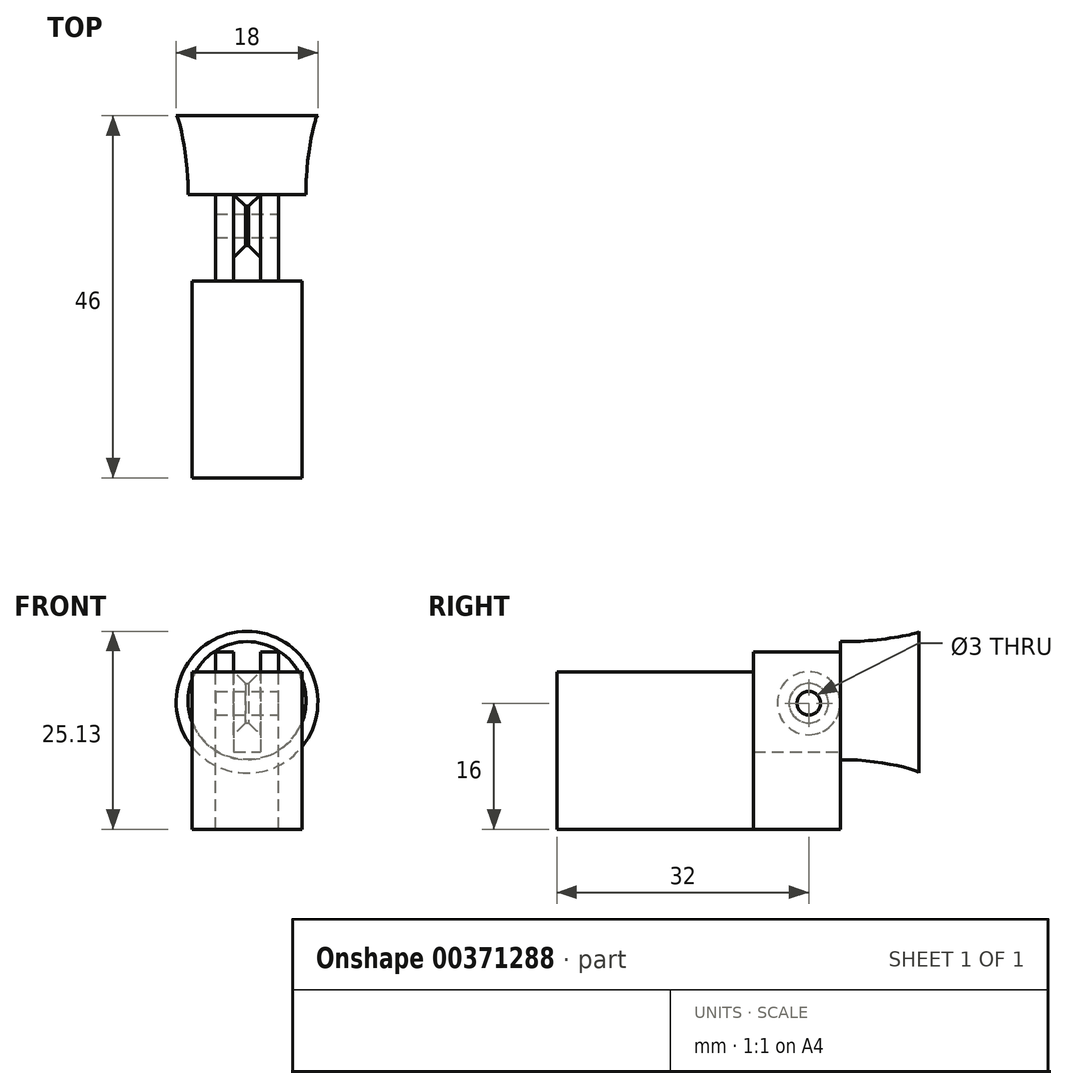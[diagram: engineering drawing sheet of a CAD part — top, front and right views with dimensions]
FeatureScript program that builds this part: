
annotation { "Feature Type Name" : "Feature", "Feature Type Description" : "" }
export const myFeature = defineFeature(function(context is Context, id is Id, definition is map)
    precondition{}
    {
        {
            var Q0;
            Q0=qCreatedBy(makeId("Front.planeOp"),FACE);
            var sketch = newSketch(context, id + "F0", { "sketchPlane" : qUnion([Q0])});
            skLineSegment(sketch, "E0", {"start": v(0, 0) * mm, "end": v(-4, 0) * mm});
            skLineSegment(sketch, "E1", {"start": v(-4, 0) * mm, "end": v(-4, 22.5) * mm});
            skLineSegment(sketch, "E2", {"start": v(-4, 22.5) * mm, "end": v(-1.7, 22.5) * mm});
            skLineSegment(sketch, "E3", {"start": v(-1.7, 22.5) * mm, "end": v(-1.7, 0) * mm, "construction": true});
            skPoint(sketch, "E3.endSnap0", {"position": v(-2, 0) * mm});
            skLineSegment(sketch, "E4", {"start": v(-1.7, 0) * mm, "end": v(-1.7, 9.8) * mm, "construction": true});
            skLineSegment(sketch, "E5", {"start": v(-1.7, 22.5) * mm, "end": v(-1.7, 9.8) * mm});
            skLineSegment(sketch, "E6", {"start": v(-1.7, 9.8) * mm, "end": v(0, 9.8) * mm});
            skLineSegment(sketch, "E7", {"start": v(0, 9.8) * mm, "end": v(0, 0) * mm});
            skSolve(sketch);
        }
        {
            var Q0;
            Q0=makeQuery(id+"F0.imprint","IMPRINT",FACE,{"disambiguationData":[TD([[makeQuery(id+"F0.imprint","IMPRINT",EDGE,{"derivedFrom":sQuery(id+"F0.wireOp",EDGE,"E0")}),-1.0]])]});
            extrude(context, id + "F1", {"entities" : qUnion([Q0]), "depth" : 11 * mm});
        }
        {
            var Q0;
            Q0=makeQuery(id+"F1.opExtrude","SWEPT_BODY",BODY,{"disambiguationData":[OSD([sQuery(id+"F0.wireOp",EDGE,"E0"),sQuery(id+"F0.wireOp",EDGE,"E1"),sQuery(id+"F0.wireOp",EDGE,"E2"),sQuery(id+"F0.wireOp",EDGE,"E5"),sQuery(id+"F0.wireOp",EDGE,"E6"),sQuery(id+"F0.wireOp",EDGE,"E7")])]});
            var Q1;
            Q1=makeQuery(id+"F1.opExtrude","SWEPT_FACE",FACE,{"disambiguationData":[OSD([sQuery(id+"F0.wireOp",EDGE,"E7")])]});
            mirror(context, id + "F2", {"operationType" : NewBodyOperationType.ADD, "entities" : qUnion([Q0]), "mirrorPlane" : qUnion([Q1])});
        }
        {
            var Q0;
            {var subQ0=makeQuery(id+"F1.opExtrude","CAP_FACE",FACE,{"disambiguationData":[OSD([sQuery(id+"F0.wireOp",EDGE,"E0"),sQuery(id+"F0.wireOp",EDGE,"E1"),sQuery(id+"F0.wireOp",EDGE,"E2"),sQuery(id+"F0.wireOp",EDGE,"E5"),sQuery(id+"F0.wireOp",EDGE,"E6"),sQuery(id+"F0.wireOp",EDGE,"E7")])],"isStart":false});Q0=makeQuery(id+"F2.boolean.opBoolean","MERGE",FACE,{"derivedFrom":[subQ0,makeQuery(id+"F2.opPattern","COPY",FACE,{"derivedFrom":subQ0,"instanceName":"1"})]});}
            var sketch = newSketch(context, id + "F3", { "sketchPlane" : qUnion([Q0])});
            skLineSegment(sketch, "E8", {"start": v(0, 0) * mm, "end": v(-7, 0) * mm, "construction": true});
            skLineSegment(sketch, "E9", {"start": v(0, 0) * mm, "end": v(-7, 0) * mm});
            skLineSegment(sketch, "E10", {"start": v(-7, 0) * mm, "end": v(-7, 20) * mm});
            skLineSegment(sketch, "E11", {"start": v(0, 0) * mm, "end": v(7, 0) * mm});
            skLineSegment(sketch, "E12", {"start": v(7, 0) * mm, "end": v(7, 20) * mm});
            skLineSegment(sketch, "E13", {"start": v(-7, 20) * mm, "end": v(7, 20) * mm});
            skSolve(sketch);
        }
        {
            var Q0;
            {var subQ3=sQuery(id+"F3.wireOp",EDGE,"E12");Q0=makeQuery(id+"F3.imprint","IMPRINT",FACE,{"disambiguationData":[TD([[makeQuery(id+"F3.imprint","IMPRINT",EDGE,{"derivedFrom":subQ3}),1.0]])]});}
            var Q1;
            {var subQ13=makeQuery(id+"F1.opExtrude","CAP_EDGE",EDGE,{"disambiguationData":[OSD([sQuery(id+"F0.wireOp",EDGE,"E6")])],"isStart":false});var subQ14=makeQuery(id+"F2.boolean.opBoolean","MERGE",EDGE,{"derivedFrom":[subQ13,makeQuery(id+"F2.opPattern","COPY",EDGE,{"derivedFrom":subQ13,"instanceName":"1"})]});Q1=makeQuery(id+"F3.imprint","IMPRINT",FACE,{"disambiguationData":[TD([[makeQuery(id+"F3.imprint","IMPRINT",EDGE,{"derivedFrom":subQ14}),-1.0]])]});}
            var Q2;
            {var subQ5=makeQuery(id+"F1.opExtrude","CAP_EDGE",EDGE,{"disambiguationData":[OSD([sQuery(id+"F0.wireOp",EDGE,"E6")])],"isStart":false});var subQ6=makeQuery(id+"F2.boolean.opBoolean","MERGE",EDGE,{"derivedFrom":[subQ5,makeQuery(id+"F2.opPattern","COPY",EDGE,{"derivedFrom":subQ5,"instanceName":"1"})]});Q2=makeQuery(id+"F3.imprint","IMPRINT",FACE,{"disambiguationData":[TD([[makeQuery(id+"F3.imprint","IMPRINT",EDGE,{"derivedFrom":subQ6}),1.0]])]});}
            var Q3;
            {var subQ3=sQuery(id+"F3.wireOp",EDGE,"E10");Q3=makeQuery(id+"F3.imprint","IMPRINT",FACE,{"disambiguationData":[TD([[makeQuery(id+"F3.imprint","IMPRINT",EDGE,{"derivedFrom":subQ3}),-1.0]])]});}
            extrude(context, id + "F4", {"entities" : qUnion([Q0, Q1, Q2, Q3]), "operationType" : NewBodyOperationType.ADD, "depth" : 25 * mm});
        }
        {
            var Q0;
            Q0=makeQuery(id+"F2.opPattern","COPY",FACE,{"derivedFrom":makeQuery(id+"F1.opExtrude","SWEPT_FACE",FACE,{"disambiguationData":[OSD([sQuery(id+"F0.wireOp",EDGE,"E1")])]}),"instanceName":"1"});
            var sketch = newSketch(context, id + "F5", { "sketchPlane" : qUnion([Q0])});
            skLineSegment(sketch, "E14", {"start": v(0, 16) * mm, "end": v(-4, 16) * mm, "construction": true});
            skLineSegment(sketch, "E15", {"start": v(-4, 16) * mm, "end": v(-4, 0) * mm, "construction": true});
            skCircle(sketch, "E16", {"center": v(-4, 16) * mm, "radius": 1.5 * mm});
            skCircle(sketch, "E17", {"center": v(-4, 16) * mm, "radius": 2.5 * mm});
            skSolve(sketch);
        }
        {
            var Q0;
            Q0=makeQuery(id+"F5.imprint","IMPRINT",FACE,{"disambiguationData":[TD([[makeQuery(id+"F5.imprint","IMPRINT",EDGE,{"derivedFrom":sQuery(id+"F5.wireOp",EDGE,"E16")}),1.0]])]});
            extrude(context, id + "F6", {"entities" : qUnion([Q0]), "operationType" : NewBodyOperationType.REMOVE, "oppositeDirection" : true, "depth" : 25 * mm});
        }
        {
            var Q0;
            Q0=makeQuery(id+"F5.imprint","IMPRINT",FACE,{"disambiguationData":[TD([[makeQuery(id+"F5.imprint","IMPRINT",EDGE,{"derivedFrom":sQuery(id+"F5.wireOp",EDGE,"E16")}),-1.0]])]});
            var Q1;
            Q1=makeQuery(id+"F1.opExtrude","SWEPT_FACE",FACE,{"disambiguationData":[OSD([sQuery(id+"F0.wireOp",EDGE,"E1")])]});
            extrude(context, id + "F7", {"entities" : qUnion([Q0]), "operationType" : NewBodyOperationType.ADD, "endBound" : BoundingType.UP_TO_SURFACE, "oppositeDirection" : true, "endBoundEntityFace" : qUnion([Q1]), "depth" : 25 * mm});
        }
        {
            var Q0;
            Q0=makeQuery(id+"F7.boolean.opBoolean","INTERSECT",EDGE,{"derivedFrom":[makeQuery(id+"F1.opExtrude","SWEPT_FACE",FACE,{"disambiguationData":[OSD([sQuery(id+"F0.wireOp",EDGE,"E5")])]}),makeQuery(id+"F7.opExtrude","SWEPT_FACE",FACE,{"disambiguationData":[OSD([sQuery(id+"F5.wireOp",EDGE,"E17")])]})]});
            chamfer(context, id + "F8", {"entities" : qUnion([Q0]), "width" : 1.5 * mm, "tangentPropagation" : true});
        }
        {
            var Q0;
            Q0=makeQuery(id+"F7.boolean.opBoolean","INTERSECT",EDGE,{"derivedFrom":[makeQuery(id+"F2.opPattern","COPY",FACE,{"derivedFrom":makeQuery(id+"F1.opExtrude","SWEPT_FACE",FACE,{"disambiguationData":[OSD([sQuery(id+"F0.wireOp",EDGE,"E5")])]}),"instanceName":"1"}),makeQuery(id+"F7.opExtrude","SWEPT_FACE",FACE,{"disambiguationData":[OSD([sQuery(id+"F5.wireOp",EDGE,"E17")])]})]});
            chamfer(context, id + "F9", {"entities" : qUnion([Q0]), "width" : 1.5 * mm, "tangentPropagation" : true});
        }
        {
            var Q0;
            {var subQ0=makeQuery(id+"F1.opExtrude","CAP_FACE",FACE,{"disambiguationData":[OSD([sQuery(id+"F0.wireOp",EDGE,"E0"),sQuery(id+"F0.wireOp",EDGE,"E1"),sQuery(id+"F0.wireOp",EDGE,"E2"),sQuery(id+"F0.wireOp",EDGE,"E5"),sQuery(id+"F0.wireOp",EDGE,"E6"),sQuery(id+"F0.wireOp",EDGE,"E7")])],"isStart":true});Q0=makeQuery(id+"F2.boolean.opBoolean","MERGE",FACE,{"derivedFrom":[subQ0,makeQuery(id+"F2.opPattern","COPY",FACE,{"derivedFrom":subQ0,"instanceName":"1"})]});}
            var sketch = newSketch(context, id + "F10", { "sketchPlane" : qUnion([Q0])});
            skCircle(sketch, "E18", {"center": v(0, 16.32) * mm, "radius": 7.5 * mm});
            skSolve(sketch);
        }
        {
            var Q0;
            {var subQ5=makeQuery(id+"F1.opExtrude","CAP_EDGE",EDGE,{"disambiguationData":[OSD([sQuery(id+"F0.wireOp",EDGE,"E0")])],"isStart":true});var subQ6=makeQuery(id+"F2.boolean.opBoolean","MERGE",EDGE,{"derivedFrom":[subQ5,makeQuery(id+"F2.opPattern","COPY",EDGE,{"derivedFrom":subQ5,"instanceName":"1"})]});Q0=makeQuery(id+"F10.imprint","IMPRINT",FACE,{"disambiguationData":[TD([[makeQuery(id+"F10.imprint","IMPRINT",EDGE,{"derivedFrom":subQ6}),1.0]])]});}
            cPlane(context, id + "F11", {"entities" : qUnion([Q0]), "cplaneType" : CPlaneType.OFFSET, "offset" : 10 * mm, "width" : 150 * mm, "height" : 150 * mm});
        }
        {
            var Q0;
            Q0=qCreatedBy(id+"F11.planeOp",FACE);
            var sketch = newSketch(context, id + "F12", { "sketchPlane" : qUnion([Q0])});
            skCircle(sketch, "E19", {"center": v(0, 16.13) * mm, "radius": 9 * mm});
            skSolve(sketch);
        }
        {
            var Q0;
            Q0=qSketchRegion(id+"F10",true);
            extrude(context, id + "F13", {"entities" : qUnion([Q0]), "depth" : 0.3 * mm});
        }
        {
            var Q1;
            Q1=makeQuery(id+"F13.opExtrude","CAP_FACE",FACE,{"disambiguationData":[OSD([sQuery(id+"F10.wireOp",EDGE,"E18")])],"isStart":false});
            var Q2;
            Q2=makeQuery(id+"F12.imprint","IMPRINT",FACE,{"disambiguationData":[TD([[makeQuery(id+"F12.imprint","IMPRINT",EDGE,{"derivedFrom":sQuery(id+"F12.wireOp",EDGE,"E19")}),1.0]])]});
            loft(context, id + "F14", {"operationType" : NewBodyOperationType.ADD, "startCondition" : LoftEndDerivativeType.MATCH_CURVATURE, "startMagnitude" : 1, "endCondition" : LoftEndDerivativeType.TANGENT_TO_PROFILE, "endMagnitude" : 1, "sheetProfilesArray" : [{ "sheetProfileEntities" : qUnion([Q1]) }, { "sheetProfileEntities" : qUnion([Q2]) }]});
        }
        {
            var Q0;
            Q0=makeQuery(id+"F14.opLoft","CAP_FACE",FACE,{"disambiguationData":[OSD([makeQuery(id+"F12.imprint","IMPRINT",FACE,{"disambiguationData":[TD([[makeQuery(id+"F12.imprint","IMPRINT",EDGE,{"derivedFrom":sQuery(id+"F12.wireOp",EDGE,"E19")}),1.0]])]})])],"isStart":true});
            cPlane(context, id + "F15", {"entities" : qUnion([Q0]), "cplaneType" : CPlaneType.OFFSET, "offset" : 25 * mm, "width" : 150 * mm, "height" : 150 * mm});
        }
    });
